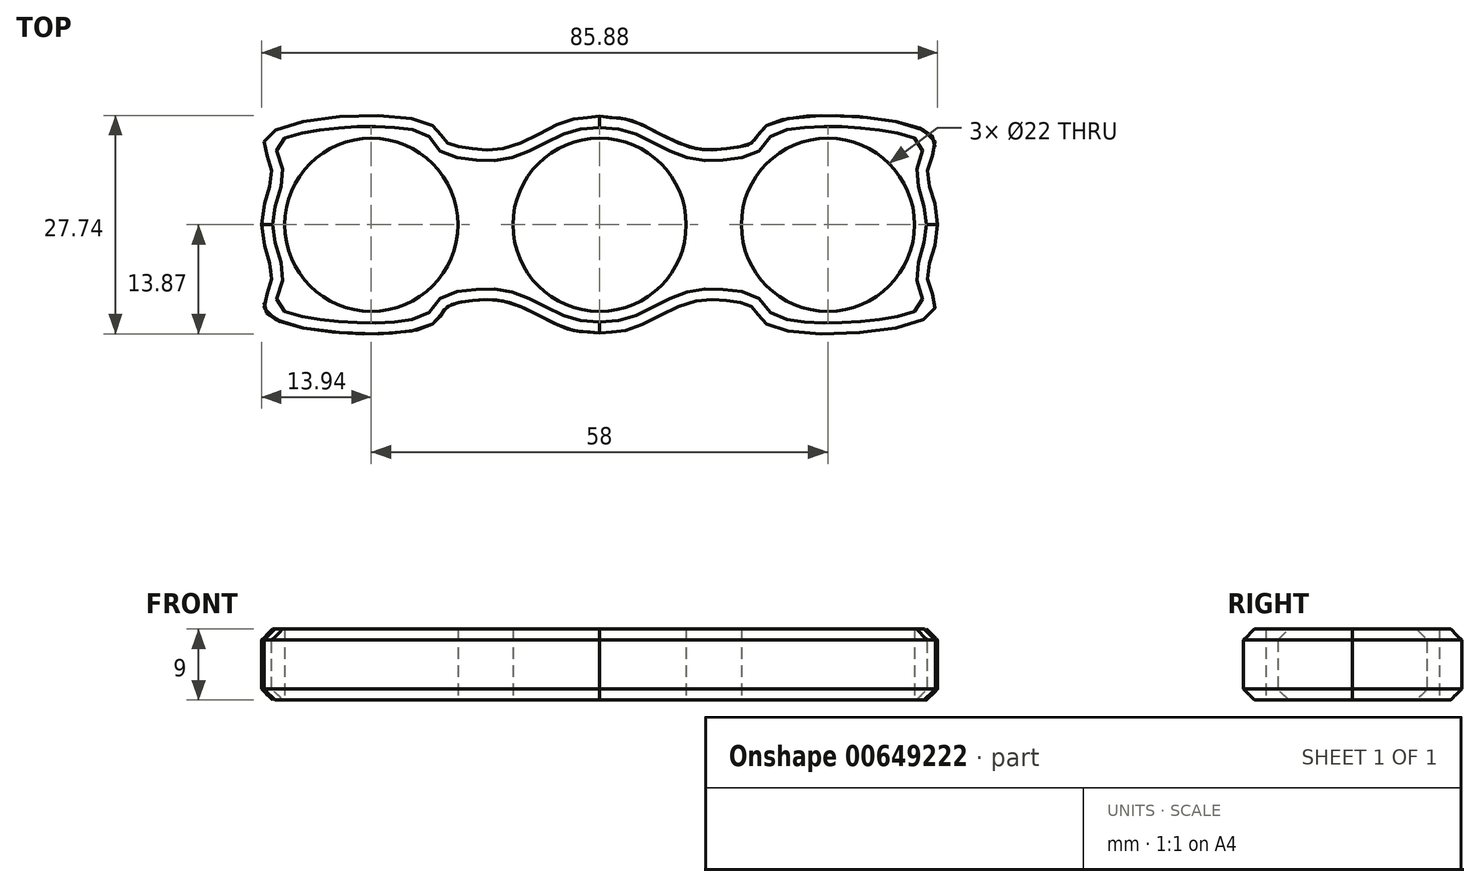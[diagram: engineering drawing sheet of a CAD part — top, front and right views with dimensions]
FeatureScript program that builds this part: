
annotation { "Feature Type Name" : "Feature", "Feature Type Description" : "" }
export const myFeature = defineFeature(function(context is Context, id is Id, definition is map)
    precondition{}
    {
        {
            var Q0;
            Q0=qCreatedBy(makeId("Top.planeOp"),FACE);
            var sketch = newSketch(context, id + "F0", { "sketchPlane" : qUnion([Q0])});
            skCircle(sketch, "E0", {"center": v(0, 0) * mm, "radius": 11 * mm});
            skCircle(sketch, "E1", {"center": v(-29, 0) * mm, "radius": 11 * mm});
            skCircle(sketch, "E2", {"center": v(29, 0) * mm, "radius": 11 * mm});
            skFitSpline(sketch, "E3", {"points": [v(-42.94, 0) * mm, v(-41.68, 7) * mm, v(-42.23, 11.3) * mm, v(-21.92, 12.98) * mm, v(-19.55, 10.59) * mm, v(-16.42, 9.7) * mm, v(-11.31, 9.92) * mm, v(-3.8, 13.31) * mm, v(0, 13.78) * mm], "startDerivative": vector(-0.59, 68.18) * mm, "endDerivative": vector(34.82, 8.13) * mm});
            skFitSpline(sketch, "E4.MirrorCS", {"points": [v(42.94, 0) * mm, v(41.68, 7) * mm, v(42.23, 11.3) * mm, v(21.92, 12.98) * mm, v(19.55, 10.59) * mm, v(16.42, 9.7) * mm, v(11.31, 9.92) * mm, v(3.8, 13.31) * mm, v(0, 13.78) * mm], "startDerivative": vector(0.59, 68.18) * mm, "endDerivative": vector(-34.82, 8.13) * mm});
            skFitSpline(sketch, "E5.MirrorCS", {"points": [v(-42.94, 0) * mm, v(-41.68, -7) * mm, v(-42.23, -11.3) * mm, v(-21.92, -12.98) * mm, v(-19.55, -10.59) * mm, v(-16.42, -9.7) * mm, v(-11.31, -9.92) * mm, v(-3.8, -13.31) * mm, v(0, -13.78) * mm], "startDerivative": vector(-0.59, -68.18) * mm, "endDerivative": vector(34.82, -8.13) * mm});
            skFitSpline(sketch, "E6.MirrorCS", {"points": [v(42.94, 0) * mm, v(41.68, -7) * mm, v(42.23, -11.3) * mm, v(21.92, -12.98) * mm, v(19.55, -10.59) * mm, v(16.42, -9.7) * mm, v(11.31, -9.92) * mm, v(3.8, -13.31) * mm, v(0, -13.78) * mm], "startDerivative": vector(0.59, -68.18) * mm, "endDerivative": vector(-34.82, -8.13) * mm});
            skSolve(sketch);
        }
        {
            var Q0;
            Q0=makeQuery(id+"F0.imprint","IMPRINT",FACE,{"disambiguationData":[TD([[makeQuery(id+"F0.imprint","IMPRINT",EDGE,{"derivedFrom":sQuery(id+"F0.wireOp",EDGE,"E0")}),-1.0]])]});
            extrude(context, id + "F1", {"entities" : qUnion([Q0]), "depth" : 9 * mm, "offsetDistance" : 25.4 * mm});
        }
        {
            var Q0;
            Q0=makeQuery(id+"F1.opExtrude","CAP_EDGE",EDGE,{"disambiguationData":[OSD([sQuery(id+"F0.wireOp",EDGE,"E3")])],"isStart":false});
            var Q1;
            Q1=makeQuery(id+"F1.opExtrude","CAP_EDGE",EDGE,{"disambiguationData":[OSD([sQuery(id+"F0.wireOp",EDGE,"E5.MirrorCS")])],"isStart":false});
            var Q2;
            Q2=makeQuery(id+"F1.opExtrude","CAP_EDGE",EDGE,{"disambiguationData":[OSD([sQuery(id+"F0.wireOp",EDGE,"E6.MirrorCS")])],"isStart":false});
            var Q3;
            Q3=makeQuery(id+"F1.opExtrude","CAP_EDGE",EDGE,{"disambiguationData":[OSD([sQuery(id+"F0.wireOp",EDGE,"E4.MirrorCS")])],"isStart":false});
            var Q4;
            Q4=makeQuery(id+"F1.opExtrude","CAP_EDGE",EDGE,{"disambiguationData":[OSD([sQuery(id+"F0.wireOp",EDGE,"E4.MirrorCS")])],"isStart":true});
            var Q5;
            Q5=makeQuery(id+"F1.opExtrude","CAP_EDGE",EDGE,{"disambiguationData":[OSD([sQuery(id+"F0.wireOp",EDGE,"E6.MirrorCS")])],"isStart":true});
            var Q6;
            Q6=makeQuery(id+"F1.opExtrude","CAP_EDGE",EDGE,{"disambiguationData":[OSD([sQuery(id+"F0.wireOp",EDGE,"E3")])],"isStart":true});
            var Q7;
            Q7=makeQuery(id+"F1.opExtrude","CAP_EDGE",EDGE,{"disambiguationData":[OSD([sQuery(id+"F0.wireOp",EDGE,"E5.MirrorCS")])],"isStart":true});
            chamfer(context, id + "F2", {"entities" : qUnion([Q0, Q1, Q2, Q3, Q4, Q5, Q6, Q7]), "width" : 1.4 * mm, "tangentPropagation" : true});
        }
    });
